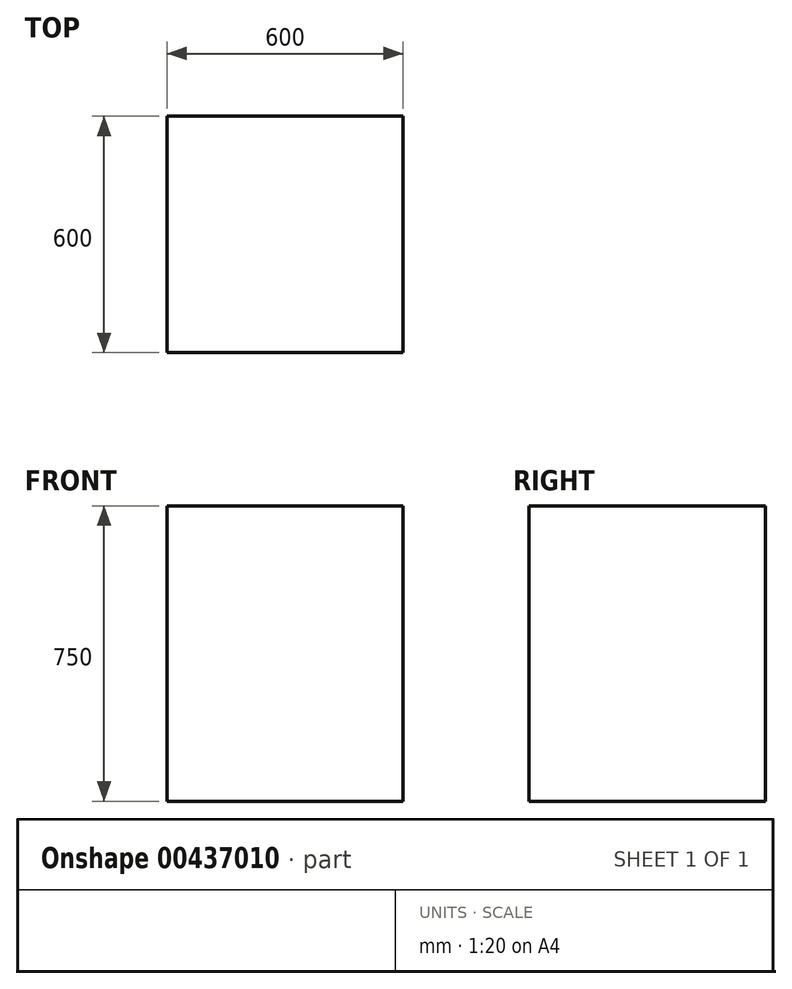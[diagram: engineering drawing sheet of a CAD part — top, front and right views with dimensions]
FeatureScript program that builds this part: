
annotation { "Feature Type Name" : "Feature", "Feature Type Description" : "" }
export const myFeature = defineFeature(function(context is Context, id is Id, definition is map)
    precondition{}
    {
        {
            var Q0;
            Q0=qCreatedBy(makeId("Right.planeOp"),FACE);
            var sketch = newSketch(context, id + "F0", { "sketchPlane" : qUnion([Q0])});
            skLineSegment(sketch, "E0.top", {"start": v(0, 750) * mm, "end": v(-600, 750) * mm});
            skLineSegment(sketch, "E0.left", {"start": v(0, 0) * mm, "end": v(0, 750) * mm});
            skLineSegment(sketch, "E0.right", {"start": v(-600, 0) * mm, "end": v(-600, 750) * mm});
            skLineSegment(sketch, "E1", {"start": v(0, 0) * mm, "end": v(-600, 0) * mm});
            skSolve(sketch);
        }
        {
            var Q0;
            Q0=qSketchRegion(id+"F0",true);
            extrude(context, id + "F1", {"entities" : qUnion([Q0]), "depth" : 600 * mm});
        }
    });
